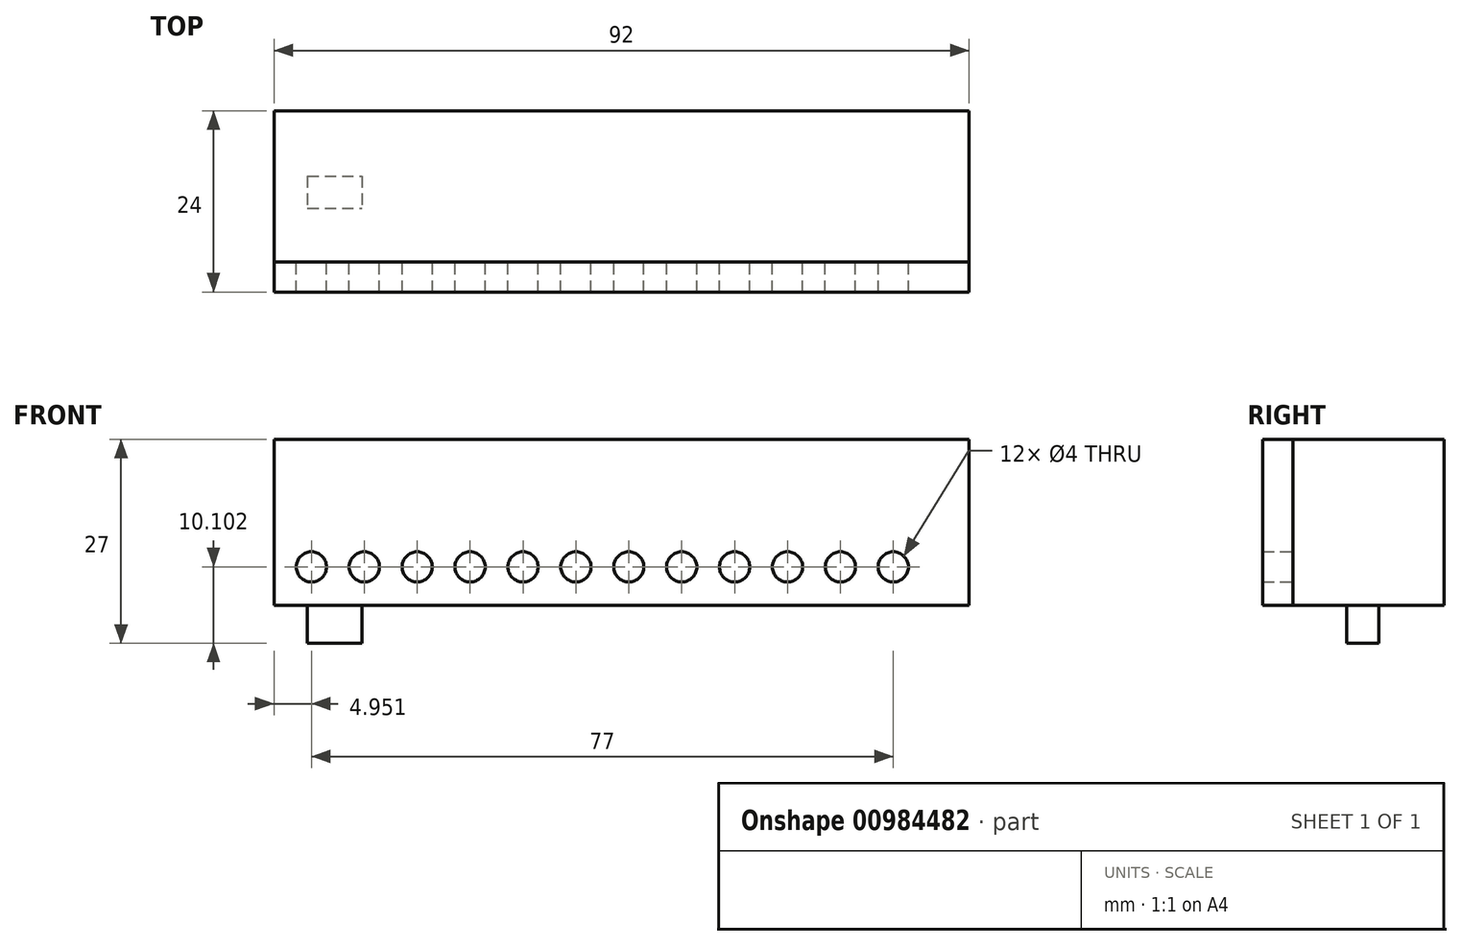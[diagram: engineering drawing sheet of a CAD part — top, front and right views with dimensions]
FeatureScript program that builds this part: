
annotation { "Feature Type Name" : "Feature", "Feature Type Description" : "" }
export const myFeature = defineFeature(function(context is Context, id is Id, definition is map)
    precondition{}
    {
        {
            var Q0;
            Q0=qCreatedBy(makeId("Front.planeOp"),FACE);
            var sketch = newSketch(context, id + "F0", { "sketchPlane" : qUnion([Q0])});
            skLineSegment(sketch, "E0.bottom", {"start": v(-71.11, 35.94) * mm, "end": v(20.89, 35.94) * mm});
            skLineSegment(sketch, "E0.top", {"start": v(-71.11, 13.94) * mm, "end": v(20.89, 13.94) * mm});
            skLineSegment(sketch, "E0.left", {"start": v(-71.11, 35.94) * mm, "end": v(-71.11, 13.94) * mm});
            skLineSegment(sketch, "E0.right", {"start": v(20.89, 35.94) * mm, "end": v(20.89, 13.94) * mm});
            skSolve(sketch);
        }
        {
            var Q0;
            Q0 = qSketchRegion(id + "F0", true);
            extrude(context, id + "F1", {"entities" : qUnion([Q0]), "depth" : 20 * mm, "offsetDistance" : 25 * mm});
        }
        {
            var Q0;
            Q0=makeQuery(id+"F1.opExtrude","CAP_FACE",FACE,{"disambiguationData":[OSD([sQuery(id+"F0.wireOp",EDGE,"E0.bottom"),sQuery(id+"F0.wireOp",EDGE,"E0.top"),sQuery(id+"F0.wireOp",EDGE,"E0.left"),sQuery(id+"F0.wireOp",EDGE,"E0.right")])],"isStart":false});
            var sketch = newSketch(context, id + "F2", { "sketchPlane" : qUnion([Q0])});
            skCircle(sketch, "E1", {"center": v(-66.16, 19.04) * mm, "radius": 2 * mm});
            skCircle(sketch, "E2", {"center": v(-59.16, 19.04) * mm, "radius": 2 * mm});
            skCircle(sketch, "E3", {"center": v(-52.16, 19.04) * mm, "radius": 2 * mm});
            skCircle(sketch, "E4", {"center": v(-45.16, 19.04) * mm, "radius": 2 * mm});
            skCircle(sketch, "E5", {"center": v(-38.16, 19.04) * mm, "radius": 2 * mm});
            skCircle(sketch, "E6", {"center": v(-31.16, 19.04) * mm, "radius": 2 * mm});
            skCircle(sketch, "E7", {"center": v(-24.16, 19.04) * mm, "radius": 2 * mm});
            skCircle(sketch, "E8", {"center": v(-17.16, 19.04) * mm, "radius": 2 * mm});
            skCircle(sketch, "E9", {"center": v(-10.16, 19.04) * mm, "radius": 2 * mm});
            skCircle(sketch, "E10", {"center": v(-3.16, 19.04) * mm, "radius": 2 * mm});
            skCircle(sketch, "E11", {"center": v(10.84, 19.04) * mm, "radius": 2 * mm});
            skCircle(sketch, "E12", {"center": v(3.84, 19.04) * mm, "radius": 2 * mm});
            skSolve(sketch);
        }
        {
            var Q0;
            Q0=makeQuery(id+"F2.imprint","IMPRINT",FACE,{"disambiguationData":[TD([[makeQuery(id+"F2.imprint","IMPRINT",EDGE,{"derivedFrom":sQuery(id+"F2.wireOp",EDGE,"E1")}),-1.0]])]});
            var Q1;
            Q1=sQuery(id+"F2.wireOp",EDGE,"E5");
            var Q2;
            Q2=sQuery(id+"F2.wireOp",EDGE,"E6");
            var Q3;
            Q3=sQuery(id+"F2.wireOp",EDGE,"E9");
            var Q4;
            Q4=sQuery(id+"F2.wireOp",EDGE,"E8");
            var Q5;
            Q5=sQuery(id+"F2.wireOp",EDGE,"E4");
            var Q6;
            Q6=sQuery(id+"F2.wireOp",EDGE,"E10");
            var Q7;
            Q7=sQuery(id+"F2.wireOp",EDGE,"E7");
            var Q8;
            Q8=sQuery(id+"F2.wireOp",EDGE,"E11");
            var Q9;
            Q9=sQuery(id+"F2.wireOp",EDGE,"E3");
            var Q10;
            Q10=sQuery(id+"F2.wireOp",EDGE,"E2");
            var Q11;
            Q11=sQuery(id+"F2.wireOp",EDGE,"E1");
            var Q12;
            Q12=sQuery(id+"F2.wireOp",EDGE,"E12");
            extrude(context, id + "F3", {"entities" : qUnion([Q0]), "surfaceEntities" : qUnion([Q1, Q2, Q3, Q4, Q5, Q6, Q7, Q8, Q9, Q10, Q11, Q12]), "depth" : 4 * mm, "offsetDistance" : 25 * mm});
        }
        {
            var Q0;
            Q0=makeQuery(id+"F1.opExtrude","SWEPT_FACE",FACE,{"disambiguationData":[OSD([sQuery(id+"F0.wireOp",EDGE,"E0.top")])]});
            var sketch = newSketch(context, id + "F4", { "sketchPlane" : qUnion([Q0])});
            skLineSegment(sketch, "E13.bottom", {"start": v(-66.68, 8.65) * mm, "end": v(-59.48, 8.65) * mm});
            skLineSegment(sketch, "E13.top", {"start": v(-66.68, 12.91) * mm, "end": v(-59.48, 12.91) * mm});
            skLineSegment(sketch, "E13.left", {"start": v(-66.68, 8.65) * mm, "end": v(-66.68, 12.91) * mm});
            skLineSegment(sketch, "E13.right", {"start": v(-59.48, 8.65) * mm, "end": v(-59.48, 12.91) * mm});
            skSolve(sketch);
        }
        {
            var Q0;
            Q0 = qSketchRegion(id + "F4", true);
            extrude(context, id + "F5", {"entities" : qUnion([Q0]), "operationType" : NewBodyOperationType.ADD, "depth" : 5 * mm, "offsetDistance" : 25 * mm});
        }
    });
